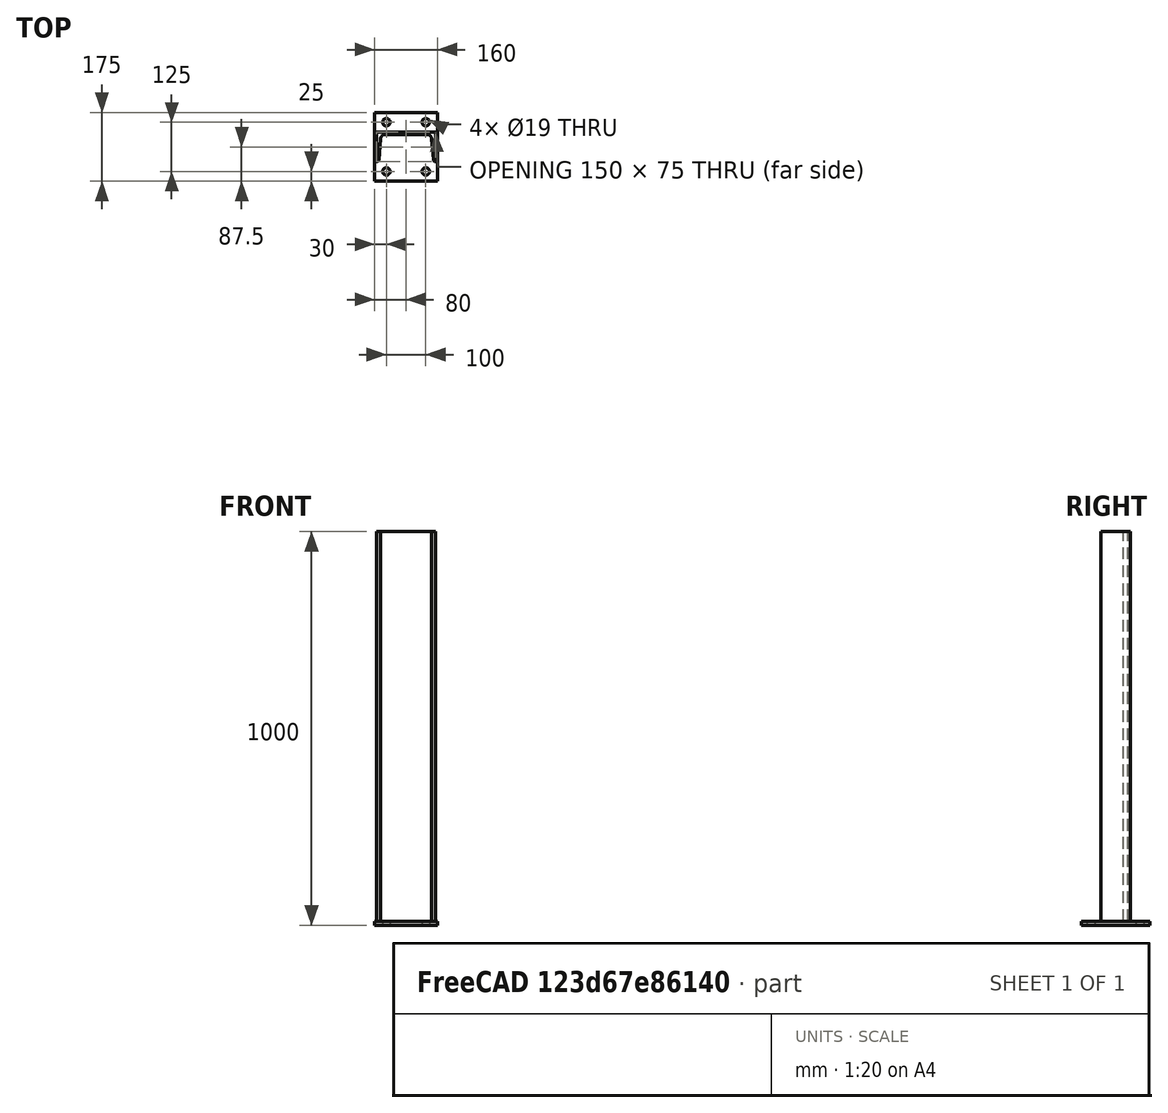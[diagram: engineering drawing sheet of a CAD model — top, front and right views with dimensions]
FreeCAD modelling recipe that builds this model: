
FCSTD DOCUMENT  (FreeCAD 0.21R33771 (Git))
Label: cvPost2
License: All rights reserved
LicenseURL: https://en.wikipedia.org/wiki/All_rights_reserved
objects: Part::FeaturePython×2, Part::Extrusion×1, Part::MultiFuse×1, App::Part×1
note: 4 computed .brp shape members not serialized (recipe doc carries the construction recipe); baked Part::Feature solids carry a one-line shape summary decoded from their .brp

FEATURE [Part::FeaturePython] BasePlate  # WARN: FeaturePython — macro-defined, semantics opaque (R4)
  B = 175
  D = 19
  H = 160
  b1 = 25
  h1 = 30
  sface = 0
FEATURE [Part::Extrusion] Extrude
  Base = -> BasePlate
  Dir = (0,0,1)
  DirMode = 2
  FaceMakerClass = Part::FaceMakerBullseye
  LengthFwd = 10
  LengthRev = 0
  Solid = true
  Symmetric = false
FEATURE [Part::FeaturePython] Channel  # WARN: FeaturePython — macro-defined, semantics opaque (R4)
  B = 75
  H = 150
  L = 1000
  Solid = true
  g0 = 7.85
  mass = 16.9049
  size = 3
  standard = SS
FEATURE [Part::MultiFuse] Fusion  label="PostC"
  Placement = pos=(0,-37.5,0) rot=(0,0,-1;1.5708rad)
  Shapes = -> [Extrude,Channel]
FEATURE [App::Part] Part  label="post"
  Group = -> [BasePlate,Channel,Extrude,Fusion]
  Origin = -> Origin
